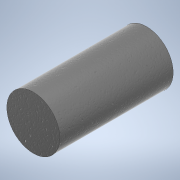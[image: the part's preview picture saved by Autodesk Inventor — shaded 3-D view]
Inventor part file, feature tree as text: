
AUTODESK INVENTOR PART (.ipt)
format: ipt  version: 2020 (Build 240168000, 168)  size: 113,152 bytes
history: native  units: mm
features: extrude x1, sketch x1
ambient origin geometry x8: Origin, YZ Plane, XZ Plane, XY Plane, X Axis, Y Axis, Z Axis, Center Point
bodies: Solid1 (feature_tree)
feature tree (2):
  extrude  "Extrusion1"  Depth=160.0mm TaperAngle=0.0deg
  sketch  "Sketch1"  dims[d0=75.0mm d1=160.0mm d2=0.0mm]
